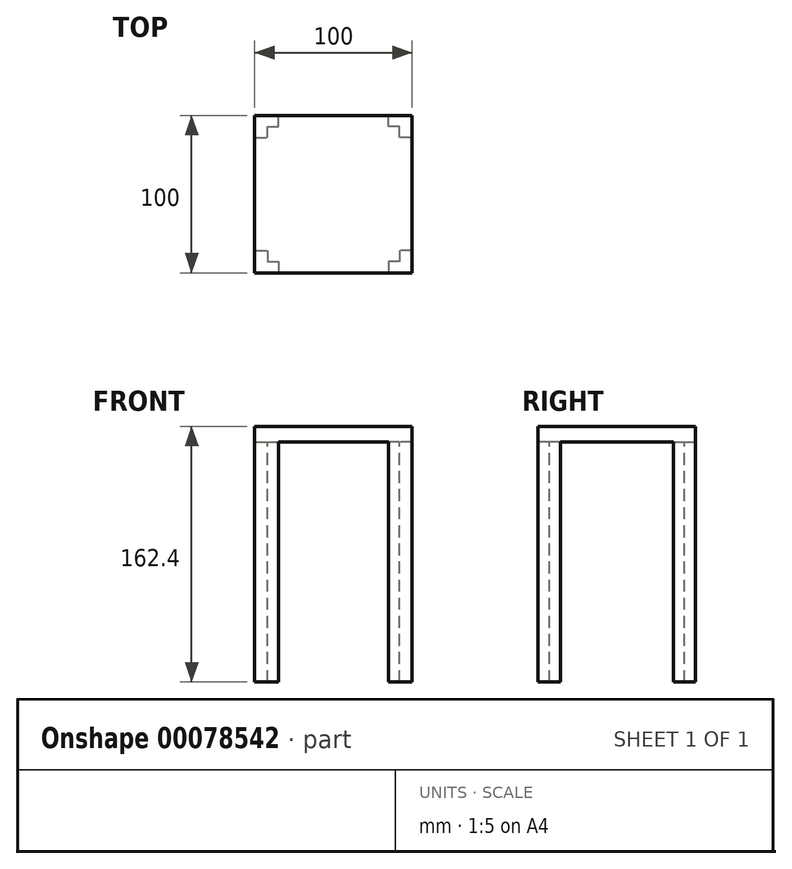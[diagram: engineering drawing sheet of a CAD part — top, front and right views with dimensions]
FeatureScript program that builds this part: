
annotation { "Feature Type Name" : "Feature", "Feature Type Description" : "" }
export const myFeature = defineFeature(function(context is Context, id is Id, definition is map)
    precondition{}
    {
        {
            var Q0;
            Q0=qCreatedBy(makeId("Top.planeOp"),FACE);
            cPlane(context, id + "F0", {"entities" : qUnion([Q0]), "cplaneType" : CPlaneType.OFFSET, "offset" : 152.4 * mm, "width" : 152.4 * mm, "height" : 152.4 * mm});
        }
        {
            var Q0;
            Q0=qCreatedBy(id+"F0.planeOp",FACE);
            var sketch = newSketch(context, id + "F1", { "sketchPlane" : qUnion([Q0])});
            skLineSegment(sketch, "E0.bottom", {"start": v(-50, 50) * mm, "end": v(50, 50) * mm});
            skLineSegment(sketch, "E0.top", {"start": v(-50, -50) * mm, "end": v(50, -50) * mm});
            skLineSegment(sketch, "E0.left", {"start": v(-50, 50) * mm, "end": v(-50, -50) * mm});
            skLineSegment(sketch, "E0.right", {"start": v(50, 50) * mm, "end": v(50, -50) * mm});
            skSolve(sketch);
        }
        {
            var Q0;
            Q0=makeQuery(id+"F1.imprint","IMPRINT",FACE,{"disambiguationData":[TD([[makeQuery(id+"F1.imprint","IMPRINT",EDGE,{"derivedFrom":sQuery(id+"F1.wireOp",EDGE,"E0.bottom")}),-1.0]])]});
            extrude(context, id + "F2", {"entities" : qUnion([Q0]), "depth" : 10 * mm});
        }
        {
            var Q0;
            Q0=makeQuery(id+"F2.opExtrude","CAP_FACE",FACE,{"disambiguationData":[OSD([sQuery(id+"F1.wireOp",EDGE,"E0.bottom"),sQuery(id+"F1.wireOp",EDGE,"E0.top"),sQuery(id+"F1.wireOp",EDGE,"E0.left"),sQuery(id+"F1.wireOp",EDGE,"E0.right")])],"isStart":true});
            var sketch = newSketch(context, id + "F3", { "sketchPlane" : qUnion([Q0])});
            skLineSegment(sketch, "E1", {"start": v(-50, 35.82) * mm, "end": v(-42, 35.82) * mm});
            skLineSegment(sketch, "E2", {"start": v(-42, 35.82) * mm, "end": v(-42, 42.87) * mm});
            skLineSegment(sketch, "E3", {"start": v(-42, 42.87) * mm, "end": v(-35, 42.87) * mm});
            skLineSegment(sketch, "E4", {"start": v(-35, 42.87) * mm, "end": v(-35, 50) * mm});
            skLineSegment(sketch, "E5", {"start": v(-35, 50) * mm, "end": v(-50, 50) * mm});
            skLineSegment(sketch, "E6", {"start": v(-50, 50) * mm, "end": v(-50, 35.82) * mm});
            skLineSegment(sketch, "E7.MirrorCS", {"start": v(50, 35.82) * mm, "end": v(42, 35.82) * mm});
            skLineSegment(sketch, "E8.MirrorCS", {"start": v(42, 35.82) * mm, "end": v(42, 42.87) * mm});
            skLineSegment(sketch, "E9.MirrorCS", {"start": v(42, 42.87) * mm, "end": v(35, 42.87) * mm});
            skLineSegment(sketch, "E10.MirrorCS", {"start": v(35, 42.87) * mm, "end": v(35, 50) * mm});
            skLineSegment(sketch, "E11.MirrorCS", {"start": v(35, 50) * mm, "end": v(50, 50) * mm});
            skLineSegment(sketch, "E12.MirrorCS", {"start": v(50, 50) * mm, "end": v(50, 35.82) * mm});
            skLineSegment(sketch, "E13.MirrorCS", {"start": v(42, -35.82) * mm, "end": v(42, -42.87) * mm});
            skLineSegment(sketch, "E14.MirrorCS", {"start": v(42, -42.87) * mm, "end": v(35, -42.87) * mm});
            skLineSegment(sketch, "E15.MirrorCS", {"start": v(-50, -35.82) * mm, "end": v(-42, -35.82) * mm});
            skLineSegment(sketch, "E16.MirrorCS", {"start": v(-42, -35.82) * mm, "end": v(-42, -42.87) * mm});
            skLineSegment(sketch, "E17.MirrorCS", {"start": v(-42, -42.87) * mm, "end": v(-35, -42.87) * mm});
            skLineSegment(sketch, "E18.MirrorCS", {"start": v(50, -35.82) * mm, "end": v(42, -35.82) * mm});
            skLineSegment(sketch, "E19.MirrorCS", {"start": v(35, -42.87) * mm, "end": v(35, -50) * mm});
            skLineSegment(sketch, "E20.MirrorCS", {"start": v(50, -50) * mm, "end": v(50, -35.82) * mm});
            skLineSegment(sketch, "E21.MirrorCS", {"start": v(35, -50) * mm, "end": v(50, -50) * mm});
            skLineSegment(sketch, "E22.MirrorCS", {"start": v(-35, -50) * mm, "end": v(-50, -50) * mm});
            skLineSegment(sketch, "E23.MirrorCS", {"start": v(-50, -50) * mm, "end": v(-50, -35.82) * mm});
            skLineSegment(sketch, "E24.MirrorCS", {"start": v(-35, -42.87) * mm, "end": v(-35, -50) * mm});
            skSolve(sketch);
        }
        {
            var Q0;
            Q0 = qSketchRegion(id + "F3", true);
            var Q1;
            Q1=qCreatedBy(makeId("Top.planeOp"),FACE);
            extrude(context, id + "F4", {"entities" : qUnion([Q0]), "operationType" : NewBodyOperationType.ADD, "endBound" : BoundingType.UP_TO_SURFACE, "endBoundEntityFace" : qUnion([Q1]), "depth" : 200 * mm});
        }
    });
